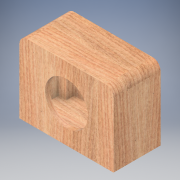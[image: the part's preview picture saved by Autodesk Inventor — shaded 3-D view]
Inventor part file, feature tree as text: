
AUTODESK INVENTOR PART (.ipt)
format: ipt  version: 2017 (Build 210142000, 142)  size: 230,912 bytes
history: native  units: in
note: dims shown in document units (in); Inventor stores cm internally (conversion verified against a paired STEP export)
features: extrude x8, sketch x8, projected_geometry x7, fillet x1
ambient origin geometry x8: Origin, YZ Plane, XZ Plane, XY Plane, X Axis, Y Axis, Z Axis, Center Point
bodies: Solid1 (feature_tree)
feature tree (24):
  extrude  "Extrusion1"  Depth=12.0in
  extrude  "Extrusion2"  Depth=0.625in
  extrude  "Extrusion3"  Depth=8.0in TaperAngle=0.0deg
  extrude  "Extrusion4"  Depth=8.0in TaperAngle=0.0deg
  extrude  "Extrusion5"  Depth=8.0in TaperAngle=0.0deg
  extrude  "Extrusion6"  Depth=0.625in TaperAngle=0.0deg
  extrude  "Extrusion7"  Depth=0.75in TaperAngle=0.0deg
  extrude  "Extrusion8"  Depth=1.0in
  fillet  "Fillet1"  Radius=1.0in
  sketch  "Sketch1"  dims[d0=6.0in d1=12.0in]
  sketch  "Sketch4"  dims[d2=0.625in d3=0.0in d4=0.625in]
  projected_geometry  "Projected Loop2"
  sketch  "Sketch5"  dims[d5=0.625in d6=8.0in d7=0.0in]
  projected_geometry  "Projected Loop3"
  sketch  "Sketch6"  dims[d8=0.625in d9=8.0in d10=0.0in]
  projected_geometry  "Projected Loop4"
  sketch  "Sketch7"  dims[d11=0.625in d12=8.0in d13=0.0in]
  projected_geometry  "Projected Loop5"
  sketch  "Sketch8"  dims[d14=8.0in d15=0.0in d16=0.625in d17=0.0in]
  projected_geometry  "Projected Loop6"
  sketch  "Sketch9"  dims[d18=5.4724in d19=0.75in d20=0.0in]
  projected_geometry  "Projected Loop7"
  sketch  "Sketch10"  dims[d21=1.0in d22=1.0in d23=1.0in d24=1.0in d25=1.0in d26=1.0in d27=1.0in d28=0.0in d29=1.0in]
  projected_geometry  "Projected Loop8"
